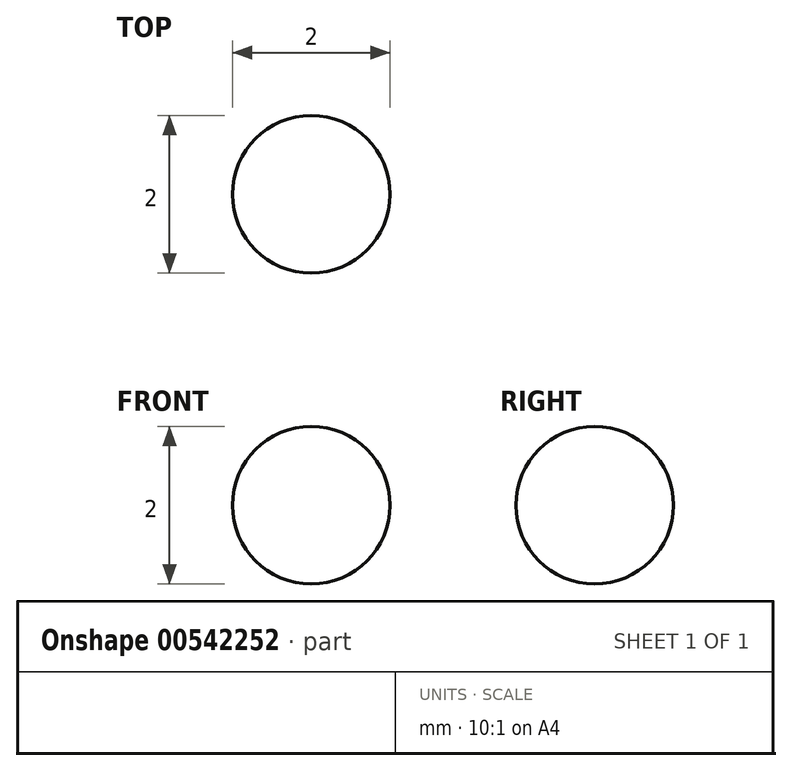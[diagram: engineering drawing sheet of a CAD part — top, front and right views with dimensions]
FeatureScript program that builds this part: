
annotation { "Feature Type Name" : "Feature", "Feature Type Description" : "" }
export const myFeature = defineFeature(function(context is Context, id is Id, definition is map)
    precondition{}
    {
        {
            var Q0;
            Q0=qCreatedBy(makeId("Front.planeOp"),FACE);
            var sketch = newSketch(context, id + "F0", { "sketchPlane" : qUnion([Q0])});
            skLineSegment(sketch, "E0", {"start": v(0, 0.6) * mm, "end": v(0, -0.6) * mm, "construction": true});
            skLineSegment(sketch, "E1", {"start": v(-0.4, 0) * mm, "end": v(0.4, 0) * mm, "construction": true});
            skArc(sketch, "E2", {"start": v(0, -1) * mm, "mid": v(1, 0) * mm, "end": v(0, 1) * mm});
            skLineSegment(sketch, "E3", {"start": v(0, 1) * mm, "end": v(0, -1) * mm});
            skSolve(sketch);
        }
        {
            var Q0;
            Q0=makeQuery(id+"F0.imprint","IMPRINT",FACE,{"disambiguationData":[TD([[makeQuery(id+"F0.imprint","IMPRINT",EDGE,{"derivedFrom":sQuery(id+"F0.wireOp",EDGE,"E2")}),1.0]])]});
            var Q1;
            Q1=sQuery(id+"F0.wireOp",EDGE,"E3");
            revolve(context, id + "F1", {"entities" : qUnion([Q0]), "axis" : qUnion([Q1]), "revolveType" : RevolveType.FULL});
        }
    });
